FCSTD DOCUMENT  (FreeCAD 0.16R6712 (Git))
Label: blah
License: All rights reserved
LicenseURL: http://en.wikipedia.org/wiki/All_rights_reserved
objects: Sketcher::SketchObject×1
note: 1 computed .brp shape members not serialized (recipe doc carries the construction recipe); baked Part::Feature solids carry a one-line shape summary decoded from their .brp

FEATURE [Sketcher::SketchObject] Sketch
  sketch-geometry (8):
    g0: LineSegment StartX=-170.727 StartY=110.138 StartZ=0 EndX=-170.727 EndY=-11.5901 EndZ=0
    g1: LineSegment StartX=-120.853 StartY=55.7438 StartZ=0 EndX=-30.2906 EndY=55.7438 EndZ=0
    g2: LineSegment StartX=-30.2906 StartY=55.7438 StartZ=0 EndX=-54.6694 EndY=-7.52315 EndZ=0
    g3: LineSegment StartX=-54.6694 StartY=-7.52315 StartZ=0 EndX=-120.853 EndY=7.1984 EndZ=0
    g4: LineSegment StartX=-120.853 StartY=7.1984 StartZ=0 EndX=-120.853 EndY=55.7438 EndZ=0
    g5: Circle CenterX=13.7307 CenterY=-14.5419 CenterZ=0 NormalX=0 NormalY=0 NormalZ=1 Radius=10
    g6: Circle CenterX=0 CenterY=0 CenterZ=0 NormalX=0 NormalY=0 NormalZ=1 Radius=30
    g7: LineSegment StartX=-170.727 StartY=45.2884 StartZ=0 EndX=-133.44 EndY=45.2884 EndZ=0
  constraints (16):
    c: Horizontal(g1)
    c: Coincident(g1,g2)
    c: Coincident(g2,g3)
    c: Coincident(g3,g4)
    c: PointOnObject(g4,g1)
    c: Vertical(g4)
    c: Perpendicular(g1,g4)
    c: Coincident(g1,g4)
    c: Equal(g2,g3)
    c: Radius(g6) = 30
    c: Radius(g5) = 10
    c: Tangent(g6,g5)
    c: Coincident(g6,g-1)
    c: PointOnObject(g7,g0)
    c: Horizontal(g7)
    c: Vertical(g0)
